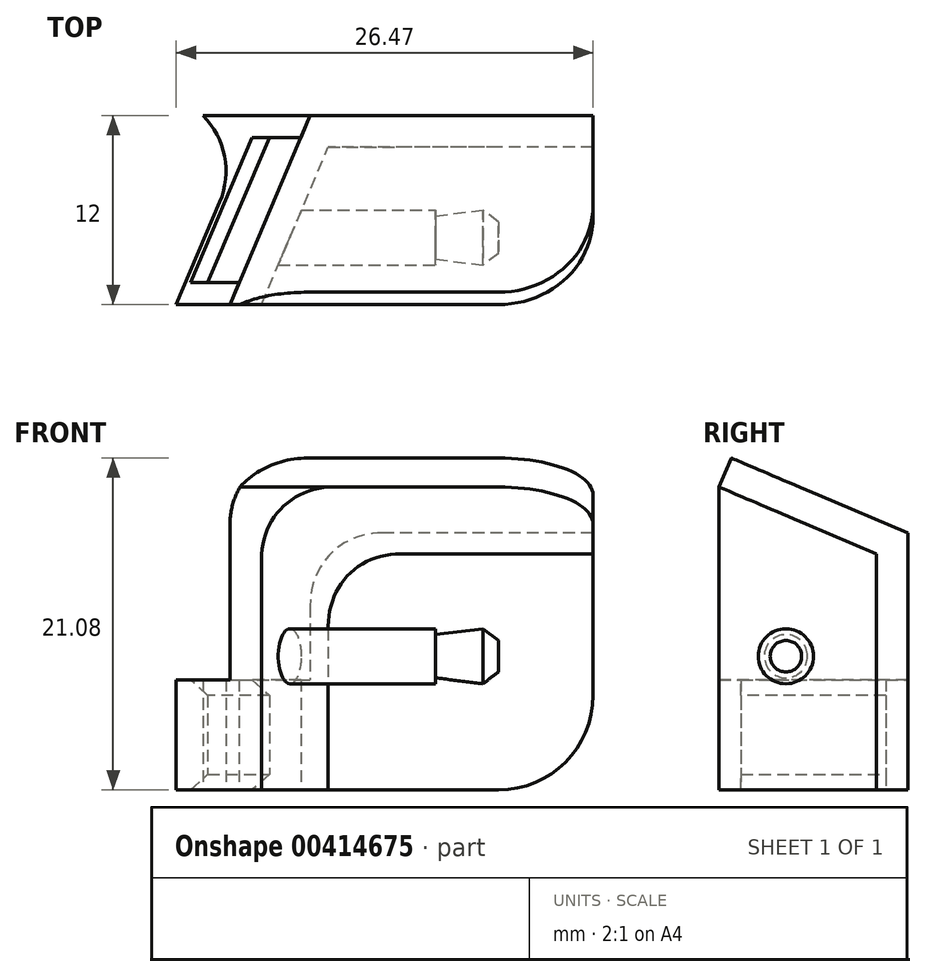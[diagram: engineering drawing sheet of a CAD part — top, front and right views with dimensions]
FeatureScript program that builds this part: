
annotation { "Feature Type Name" : "Feature", "Feature Type Description" : "" }
export const myFeature = defineFeature(function(context is Context, id is Id, definition is map)
    precondition{}
    {
        {
            var Q0;
            Q0=qCreatedBy(makeId("Front.planeOp"),FACE);
            var sketch = newSketch(context, id + "F0", { "sketchPlane" : qUnion([Q0])});
            skLineSegment(sketch, "E0", {"start": v(0, 0) * mm, "end": v(-14, 0) * mm, "construction": true});
            skLineSegment(sketch, "E1", {"start": v(-14, 1.75) * mm, "end": v(-4, 1.75) * mm});
            skLineSegment(sketch, "E2", {"start": v(-4, 1.75) * mm, "end": v(-4, 1.38) * mm});
            skLineSegment(sketch, "E3", {"start": v(-4, 1.38) * mm, "end": v(-1, 1.75) * mm});
            skLineSegment(sketch, "E4", {"start": v(-1, 1.75) * mm, "end": v(0, 1) * mm});
            skLineSegment(sketch, "E5", {"start": v(-14, 1.75) * mm, "end": v(-14, 0) * mm});
            skLineSegment(sketch, "E6", {"start": v(0, 1) * mm, "end": v(0, 0) * mm});
            skLineSegment(sketch, "E7", {"start": v(0, 0) * mm, "end": v(-14, 0) * mm});
            skSolve(sketch);
        }
        {
            var Q0;
            Q0=makeQuery(id+"F0.imprint","IMPRINT",FACE,{"disambiguationData":[TD([[makeQuery(id+"F0.imprint","IMPRINT",EDGE,{"derivedFrom":sQuery(id+"F0.wireOp",EDGE,"E1")}),-1.0]])]});
            var Q1;
            Q1=sQuery(id+"F0.wireOp",EDGE,"E7");
            revolve(context, id + "F1", {"entities" : qUnion([Q0]), "axis" : qUnion([Q1]), "revolveType" : RevolveType.FULL});
        }
        {
            var Q0;
            Q0=makeQuery(id+"F1.opRevolve","SWEPT_FACE",FACE,{"disambiguationData":[OSD([sQuery(id+"F0.wireOp",EDGE,"E5")])]});
            cPlane(context, id + "F2", {"entities" : qUnion([Q0]), "cplaneType" : CPlaneType.OFFSET, "offset" : 0 * mm, "width" : 150 * mm, "height" : 150 * mm});
        }
        {
            var Q0;
            Q0=qCreatedBy(id+"F2.planeOp",FACE);
            var sketch = newSketch(context, id + "F3", { "sketchPlane" : qUnion([Q0])});
            skPoint(sketch, "E8", {"position": v(0, 1.75) * mm});
            skLineSegment(sketch, "E9", {"start": v(-3.34, 10.75) * mm, "end": v(3.74, 10.75) * mm, "construction": true});
            skPoint(sketch, "E10", {"position": v(1.75, 0) * mm});
            skLineSegment(sketch, "E11", {"start": v(4.25, 10.75) * mm, "end": v(-5.75, 6.5) * mm});
            skPoint(sketch, "E12", {"position": v(-1.75, 0) * mm});
            skLineSegment(sketch, "E13", {"start": v(-5.75, 6.5) * mm, "end": v(-5.75, -8.5) * mm});
            skLineSegment(sketch, "E14", {"start": v(-5.75, -8.5) * mm, "end": v(-7.75, -8.5) * mm});
            skLineSegment(sketch, "E15", {"start": v(-7.75, -8.5) * mm, "end": v(-7.75, 7.83) * mm});
            skLineSegment(sketch, "E16", {"start": v(-7.75, 7.83) * mm, "end": v(3.47, 12.6) * mm});
            skLineSegment(sketch, "E17", {"start": v(3.47, 12.6) * mm, "end": v(4.25, 10.75) * mm});
            skSolve(sketch);
        }
        {
            var Q0;
            Q0=makeQuery(id+"F3.imprint","IMPRINT",FACE,{"disambiguationData":[TD([[makeQuery(id+"F3.imprint","IMPRINT",EDGE,{"derivedFrom":sQuery(id+"F3.wireOp",EDGE,"E11")}),-1.0]])]});
            var Q1;
            Q1 = qSketchRegion(id + "F9", true);
            extrude(context, id + "F4", {"entities" : qUnion([Q0, Q1]), "oppositeDirection" : true, "depth" : 20 * mm, "hasSecondDirection" : true, "secondDirectionOppositeDirection" : false, "secondDirectionDepth" : 5 * mm});
        }
        {
            var Q0;
            Q0=makeQuery(id+"F4.opExtrude","SWEPT_FACE",FACE,{"disambiguationData":[OSD([sQuery(id+"F3.wireOp",EDGE,"E15")])]});
            var sketch = newSketch(context, id + "F5", { "sketchPlane" : qUnion([Q0])});
            skArc(sketch, "E18", {"start": v(-6, -2.5) * mm, "mid": v(-4.24, -6.74) * mm, "end": v(0, -8.5) * mm});
            skLineSegment(sketch, "E19", {"start": v(-6, -2.5) * mm, "end": v(-6, -8.5) * mm});
            skLineSegment(sketch, "E20", {"start": v(-6, -8.5) * mm, "end": v(0, -8.5) * mm});
            skSolve(sketch);
        }
        {
            var Q0;
            Q0=makeQuery(id+"F5.imprint","IMPRINT",FACE,{"disambiguationData":[TD([[makeQuery(id+"F5.imprint","IMPRINT",EDGE,{"derivedFrom":sQuery(id+"F5.wireOp",EDGE,"E18")}),-1.0]])]});
            var Q1;
            Q1=makeQuery(id+"F4.opExtrude","SWEPT_FACE",FACE,{"disambiguationData":[OSD([sQuery(id+"F3.wireOp",EDGE,"E13")])]});
            extrude(context, id + "F6", {"entities" : qUnion([Q0]), "operationType" : NewBodyOperationType.REMOVE, "endBound" : BoundingType.UP_TO_SURFACE, "oppositeDirection" : true, "endBoundEntityFace" : qUnion([Q1]), "depth" : 25 * mm});
        }
        {
            var Q0;
            Q0=makeQuery(id+"F4.opExtrude","SWEPT_FACE",FACE,{"disambiguationData":[OSD([sQuery(id+"F3.wireOp",EDGE,"E16")])]});
            var sketch = newSketch(context, id + "F7", { "sketchPlane" : qUnion([Q0])});
            skArc(sketch, "E21", {"start": v(0, -8.11) * mm, "mid": v(4.24, -6.36) * mm, "end": v(6, -2.11) * mm});
            skLineSegment(sketch, "E22", {"start": v(0, -8.11) * mm, "end": v(6, -8.11) * mm});
            skLineSegment(sketch, "E23", {"start": v(6, -8.11) * mm, "end": v(6, -2.11) * mm});
            skSolve(sketch);
        }
        {
            var Q0;
            Q0=makeQuery(id+"F7.imprint","IMPRINT",FACE,{"disambiguationData":[TD([[makeQuery(id+"F7.imprint","IMPRINT",EDGE,{"derivedFrom":sQuery(id+"F7.wireOp",EDGE,"E21")}),-1.0]])]});
            var Q1;
            Q1=makeQuery(id+"F4.opExtrude","SWEPT_FACE",FACE,{"disambiguationData":[OSD([sQuery(id+"F3.wireOp",EDGE,"E11")])]});
            extrude(context, id + "F8", {"entities" : qUnion([Q0]), "operationType" : NewBodyOperationType.REMOVE, "endBound" : BoundingType.UP_TO_SURFACE, "oppositeDirection" : true, "endBoundEntityFace" : qUnion([Q1]), "depth" : 25 * mm});
        }
        {
            var Q0;
            Q0=makeQuery(id+"F4.opExtrude","SWEPT_FACE",FACE,{"disambiguationData":[OSD([sQuery(id+"F3.wireOp",EDGE,"E14")])]});
            var sketch = newSketch(context, id + "F9", { "sketchPlane" : qUnion([Q0])});
            skLineSegment(sketch, "E24", {"start": v(-14, -13.57) * mm, "end": v(-14, 1.37) * mm, "construction": true});
            skLineSegment(sketch, "E25", {"start": v(-12.19, -1.75) * mm, "end": v(-19.07, -1.75) * mm, "construction": true});
            skLineSegment(sketch, "E26", {"start": v(-9.97, -7.75) * mm, "end": v(-15.06, 4.25) * mm});
            skLineSegment(sketch, "E27", {"start": v(-15.06, 4.25) * mm, "end": v(-17.06, 4.25) * mm});
            skLineSegment(sketch, "E28", {"start": v(-17.06, 4.25) * mm, "end": v(-11.97, -7.75) * mm});
            skLineSegment(sketch, "E29", {"start": v(-11.97, -7.75) * mm, "end": v(-9.97, -7.75) * mm});
            skLineSegment(sketch, "E30", {"start": v(-11.97, -7.75) * mm, "end": v(-19, -7.75) * mm});
            skLineSegment(sketch, "E31", {"start": v(-19, -7.75) * mm, "end": v(-19, 4.25) * mm});
            skLineSegment(sketch, "E32", {"start": v(-19, 4.25) * mm, "end": v(-17.06, 4.25) * mm});
            skSolve(sketch);
        }
        {
            var Q0;
            {var subQ0=sQuery(id+"F9.wireOp",EDGE,"E32");Q0=makeQuery(id+"F9.imprint","IMPRINT",FACE,{"disambiguationData":[TD([[makeQuery(id+"F9.imprint","IMPRINT",EDGE,{"derivedFrom":subQ0}),-1.0]])]});}
            var Q1;
            {var subQ0=sQuery(id+"F9.wireOp",EDGE,"E30");Q1=makeQuery(id+"F9.imprint","IMPRINT",FACE,{"disambiguationData":[TD([[makeQuery(id+"F9.imprint","IMPRINT",EDGE,{"derivedFrom":subQ0}),-1.0]])]});}
            extrude(context, id + "F10", {"entities" : qUnion([Q0, Q1]), "operationType" : NewBodyOperationType.REMOVE, "oppositeDirection" : true, "depth" : 25 * mm});
        }
        {
            var Q0;
            {var subQ0=sQuery(id+"F9.wireOp",EDGE,"E29");Q0=makeQuery(id+"F9.imprint","IMPRINT",FACE,{"disambiguationData":[TD([[makeQuery(id+"F9.imprint","IMPRINT",EDGE,{"derivedFrom":subQ0}),-1.0]])]});}
            var Q1;
            {var subQ0=sQuery(id+"F9.wireOp",EDGE,"E27");Q1=makeQuery(id+"F9.imprint","IMPRINT",FACE,{"disambiguationData":[TD([[makeQuery(id+"F9.imprint","IMPRINT",EDGE,{"derivedFrom":subQ0}),1.0]])]});}
            var Q2;
            Q2=makeQuery(id+"F4.opExtrude","SWEPT_FACE",FACE,{"disambiguationData":[OSD([sQuery(id+"F3.wireOp",EDGE,"E16")])]});
            extrude(context, id + "F11", {"entities" : qUnion([Q0, Q1]), "operationType" : NewBodyOperationType.ADD, "endBound" : BoundingType.UP_TO_SURFACE, "oppositeDirection" : true, "endBoundEntityFace" : qUnion([Q2]), "depth" : 25 * mm});
        }
        {
            var Q0;
            {var subQ0=makeQuery(id+"F11.opExtrude","SWEPT_FACE",FACE,{"disambiguationData":[OSD([sQuery(id+"F9.wireOp",EDGE,"E26")])]});var subQ1=sQuery(id+"F3.wireOp",EDGE,"E16");Q0=makeQuery(id+"F11.boolean.opBoolean","SPLIT",FACE,{"disambiguationData":[TD([makeQuery(id+"F4.opExtrude","SWEPT_FACE",FACE,{"disambiguationData":[OSD([subQ1])]})])],"derivedFrom":subQ0});}
            var sketch = newSketch(context, id + "F12", { "sketchPlane" : qUnion([Q0])});
            skLineSegment(sketch, "E33", {"start": v(-8.95, 12.6) * mm, "end": v(-9.8, 12.92) * mm});
            skLineSegment(sketch, "E34", {"start": v(-9.8, 12.92) * mm, "end": v(-9.8, 10.75) * mm});
            skLineSegment(sketch, "E35", {"start": v(-9.8, 10.75) * mm, "end": v(-8.95, 12.6) * mm});
            skSolve(sketch);
        }
        {
            var Q0;
            Q0=makeQuery(id+"F4.opExtrude","CAP_FACE",FACE,{"disambiguationData":[OSD([sQuery(id+"F3.wireOp",EDGE,"E11"),sQuery(id+"F3.wireOp",EDGE,"E13"),sQuery(id+"F3.wireOp",EDGE,"E14"),sQuery(id+"F3.wireOp",EDGE,"E15"),sQuery(id+"F3.wireOp",EDGE,"E16"),sQuery(id+"F3.wireOp",EDGE,"E17")])],"isStart":false});
            var sketch = newSketch(context, id + "F13", { "sketchPlane" : qUnion([Q0])});
            skLineSegment(sketch, "E36", {"start": v(-3.47, 12.6) * mm, "end": v(-4.25, 12.92) * mm});
            skLineSegment(sketch, "E37", {"start": v(-4.25, 12.92) * mm, "end": v(-4.25, 10.75) * mm});
            skLineSegment(sketch, "E38", {"start": v(-4.25, 10.75) * mm, "end": v(-3.47, 12.6) * mm});
            skSolve(sketch);
        }
        {
            var Q0;
            Q0=makeQuery(id+"F13.imprint","IMPRINT",FACE,{"disambiguationData":[TD([[makeQuery(id+"F13.imprint","IMPRINT",EDGE,{"derivedFrom":sQuery(id+"F13.wireOp",EDGE,"E36")}),1.0]])]});
            var Q1;
            {var subQ0=sQuery(id+"F9.wireOp",EDGE,"E28");Q1=makeQuery(id+"F11.boolean.opBoolean","MERGE",FACE,{"derivedFrom":[makeQuery(id+"F10.boolean.opBoolean","COPY",FACE,{"derivedFrom":makeQuery(id+"F10.opExtrude","SWEPT_FACE",FACE,{"disambiguationData":[OSD([subQ0])]})}),makeQuery(id+"F11.opExtrude","SWEPT_FACE",FACE,{"disambiguationData":[OSD([subQ0])]})]});}
            extrude(context, id + "F14", {"entities" : qUnion([Q0]), "operationType" : NewBodyOperationType.REMOVE, "endBound" : BoundingType.UP_TO_SURFACE, "oppositeDirection" : true, "endBoundEntityFace" : qUnion([Q1]), "depth" : 25 * mm});
        }
        {
            var Q0;
            Q0=makeQuery(id+"F11.boolean.opBoolean","MERGE",FACE,{"derivedFrom":[makeQuery(id+"F4.opExtrude","SWEPT_FACE",FACE,{"disambiguationData":[OSD([sQuery(id+"F3.wireOp",EDGE,"E14")])]}),makeQuery(id+"F11.opExtrude","CAP_FACE",FACE,{"disambiguationData":[OSD([sQuery(id+"F9.wireOp",EDGE,"E26"),sQuery(id+"F9.wireOp",EDGE,"E27"),sQuery(id+"F9.wireOp",EDGE,"E28"),sQuery(id+"F9.wireOp",EDGE,"E29")])],"isStart":true})]});
            var sketch = newSketch(context, id + "F15", { "sketchPlane" : qUnion([Q0])});
            skLineSegment(sketch, "E39", {"start": v(-11.97, -7.75) * mm, "end": v(-15.38, -7.75) * mm});
            skLineSegment(sketch, "E40", {"start": v(-17.71, -2.26) * mm, "end": v(-20.47, 4.25) * mm});
            skLineSegment(sketch, "E41", {"start": v(-20.47, 4.25) * mm, "end": v(-17.06, 4.25) * mm});
            skLineSegment(sketch, "E42", {"start": v(-17.06, 4.25) * mm, "end": v(-11.97, -7.75) * mm});
            skPoint(sketch, "E43", {"position": v(-14.51, -1.75) * mm});
            skPoint(sketch, "E44", {"position": v(-16.47, 2.85) * mm});
            skPoint(sketch, "E45", {"position": v(-12.56, -6.35) * mm});
            skLineSegment(sketch, "E46", {"start": v(-12.56, -6.35) * mm, "end": v(-14.56, -6.35) * mm});
            skLineSegment(sketch, "E47", {"start": v(-14.56, -6.35) * mm, "end": v(-18.47, 2.85) * mm});
            skLineSegment(sketch, "E48", {"start": v(-18.47, 2.85) * mm, "end": v(-16.47, 2.85) * mm});
            skLineSegment(sketch, "E49", {"start": v(-15.38, -7.75) * mm, "end": v(-23.77, -7.75) * mm, "construction": true});
            skLineSegment(sketch, "E50", {"start": v(-20.47, 4.25) * mm, "end": v(-27.82, 4.25) * mm, "construction": true});
            skPoint(sketch, "E51", {"position": v(-17.71, -2.26) * mm});
            skPoint(sketch, "E52", {"position": v(-20.81, -7.75) * mm});
            skPoint(sketch, "E53", {"position": v(-25.9, 4.25) * mm});
            skLineSegment(sketch, "E54", {"start": v(-20.81, -7.75) * mm, "end": v(-25.9, 4.25) * mm, "construction": true});
            skPoint(sketch, "E55", {"position": v(-22.31, -4.21) * mm});
            skPoint(sketch, "E56", {"position": v(-20.36, -8.81) * mm});
            skPoint(sketch, "E57", {"position": v(-24.27, 0.4) * mm});
            skArc(sketch, "E58", {"start": v(-18.78, -7.75) * mm, "mid": v(-17.4, -5.17) * mm, "end": v(-17.71, -2.26) * mm});
            skPoint(sketch, "E59", {"position": v(-16.51, -1.75) * mm});
            skLineSegment(sketch, "E60", {"start": v(-16.51, -1.75) * mm, "end": v(-18.36, -2.53) * mm, "construction": true});
            skLineSegment(sketch, "E61", {"start": v(-18.78, -7.75) * mm, "end": v(-15.38, -7.75) * mm});
            skSolve(sketch);
        }
        {
            var Q0;
            {var subQ3=sQuery(id+"F15.wireOp",EDGE,"E39");Q0=makeQuery(id+"F15.imprint","IMPRINT",FACE,{"disambiguationData":[TD([[makeQuery(id+"F15.imprint","IMPRINT",EDGE,{"derivedFrom":subQ3}),-1.0]])]});}
            extrude(context, id + "F16", {"entities" : qUnion([Q0]), "operationType" : NewBodyOperationType.ADD, "oppositeDirection" : true, "depth" : 7 * mm});
        }
        {
            var Q0;
            Q0=makeQuery(id+"F16.opExtrude","CAP_EDGE",EDGE,{"disambiguationData":[OSD([sQuery(id+"F15.wireOp",EDGE,"E47")])],"isStart":false});
            var Q1;
            Q1=makeQuery(id+"F16.opExtrude","CAP_EDGE",EDGE,{"disambiguationData":[OSD([sQuery(id+"F15.wireOp",EDGE,"E47")])],"isStart":true});
            chamfer(context, id + "F17", {"entities" : qUnion([Q0, Q1]), "width" : 1 * mm, "tangentPropagation" : true});
        }
        {
            var Q0;
            Q0=makeQuery(id+"F11.boolean.opBoolean","INTERSECT",EDGE,{"derivedFrom":[makeQuery(id+"F4.opExtrude","SWEPT_FACE",FACE,{"disambiguationData":[OSD([sQuery(id+"F3.wireOp",EDGE,"E11")])]}),makeQuery(id+"F11.opExtrude","SWEPT_FACE",FACE,{"disambiguationData":[OSD([sQuery(id+"F9.wireOp",EDGE,"E26")])]})]});
            var Q1;
            {var subQ0=sQuery(id+"F9.wireOp",EDGE,"E28");Q1=makeQuery(id+"F11.boolean.opBoolean","MERGE",EDGE,{"derivedFrom":[makeQuery(id+"F10.boolean.opBoolean","INTERSECT",EDGE,{"derivedFrom":[makeQuery(id+"F4.opExtrude","SWEPT_FACE",FACE,{"disambiguationData":[OSD([sQuery(id+"F3.wireOp",EDGE,"E16")])]}),makeQuery(id+"F10.opExtrude","SWEPT_FACE",FACE,{"disambiguationData":[OSD([subQ0])]})]}),makeQuery(id+"F11.opExtrude","CAP_EDGE",EDGE,{"disambiguationData":[OSD([subQ0])],"isStart":false})]});}
            fillet(context, id + "F18", {"entities" : qUnion([Q0, Q1]), "tangentPropagation" : true, "radius" : 5 * mm, "defaultsChanged" : false, "vertexSettings" : [], "allowEdgeOverflow" : false});
        }
    });
